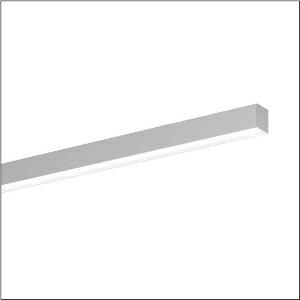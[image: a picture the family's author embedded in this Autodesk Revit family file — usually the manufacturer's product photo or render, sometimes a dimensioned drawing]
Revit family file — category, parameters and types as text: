
# Revit family: silica_r__21_51mx20da32sb_8410
name_source: partatom
category: Lighting Fixtures
units: mm (PartAtom-declared; Revit-internal decimal feet)

## family parameters
Cut with Voids When Loaded = No
Host = Face
Light Source = No
Part Type = Normal
Room Calculation Point = No
Round Connector Dimension = Use Diameter
Shared = No

## types (1)
- --- (1 x LED, 2400 lm, 16.1 W, 3000K)
    Apparent Load = 16 VA
    CIE Flux Codes = 48 79 96 100 100
    Color Rendering = 80
    Color Temperature = 3000K
    Default Elevation = 1800 mm
    Description = Silica® 21, office luminaire, primary optical cover: cover, of PMMA, opal, light emission: direct distribution, primary light characteristic: symmetric, installation type: surface-mounted, LED, rated luminous flux: 2.400lm, luminous efficacy: 149lm/W, light colour: 830, colour temperature: 3000K, with terminal, 3+2-pole, max. 2.5mm², mains connection: 220..240V, AC, 50/60Hz, rated input power: 16.1W, luminaire housing, of aluminium, metallic grey (RAL 9006), length: 1.204mm, width: 53mm, height: 53mm, protection rating (complete): IP20, insulation class (complete): insulation class I (protective earthing), certification: CE, permissible operating ambient temperature: 0..+35°C, standard: EN 50419, packaging unit: 1 piece
    Height = 0 mm  [stored 0 ft]
    Lamp = 1 x LED
    Lamp Light Flux = 2400 lm
    Lamp Power = 16.1 W
    Lamp count = 1
    Length = 1204 mm
    Luminous efficacy = 149 lm/W
    Manufacturer = Siteco
    ModVariant = No
    Model = 51MX20DA32SB
    Mounting Place = Ceiling
    Mounting Type = Recessed
    Number of Poles = 1
    OnlyDefault = Yes
    Power Factor = 1
    Product Name = Silica® 21
    Product group = office luminaire | ceiling recessed
    ProductGroupID = 401
    Protection Class = Protection class I
    Protection Degree = IP 20
    RLX_Detail_Level = 1
    RLX_Emergency_Light_Flux = 0 lm
    RLX_Emergency_Type = 0
    RLX_Emergency_Type_DB = No
    RlxData = <blob elided: 26277 chars, md5=ecbaafc0>
    Socket = socket
    Standby Power = 0 W
    System Light Flux = 2400 lm
    System Power = 16 W
    Type Comments = factory setting: luminous flux: 100 % | dim-lin: 254 | 233 mA
    Type Image = l_1297768.jpg
    URL = http://relux.com
    VarID = @adj_048169
    Voltage = 0 V
    Weight = 0.00 kg
    Width = 53 mm

note: [stored X ft] marks values corroborated as IEEE doubles in the binary element streams (Revit-internal decimal feet)

## geometry (parser evidence)
native form markers: Blend x4, Sweep x12
no freeform markers — native parametric forms only
